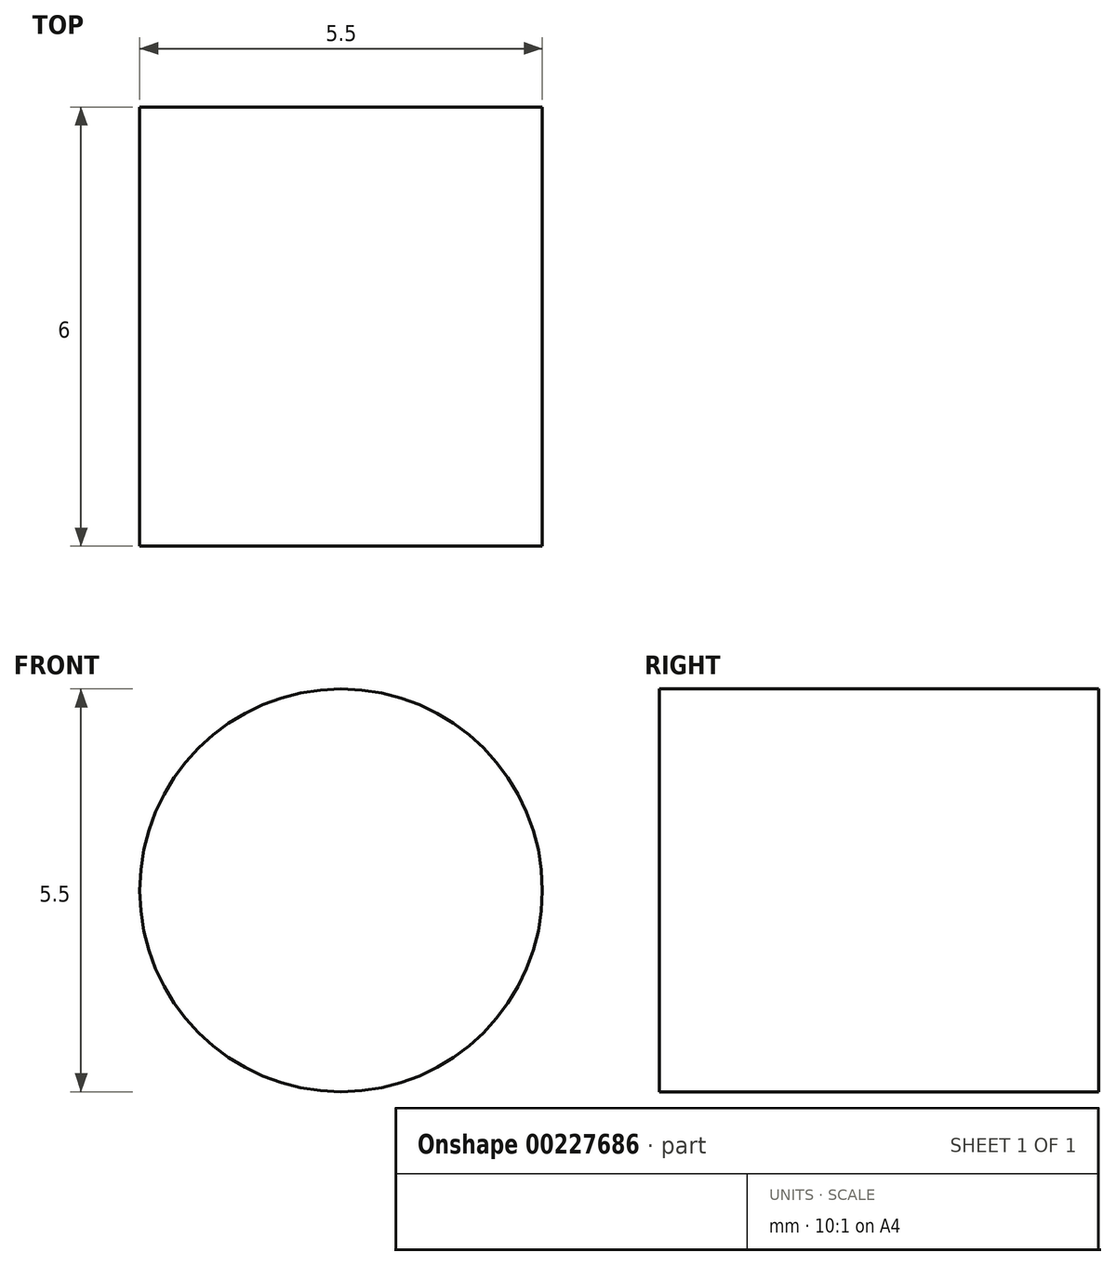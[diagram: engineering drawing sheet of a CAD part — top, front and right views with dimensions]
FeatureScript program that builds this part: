
annotation { "Feature Type Name" : "Feature", "Feature Type Description" : "" }
export const myFeature = defineFeature(function(context is Context, id is Id, definition is map)
    precondition{}
    {
        {
            var Q0;
            Q0=qCreatedBy(makeId("Front.planeOp"),FACE);
            var sketch = newSketch(context, id + "F0", { "sketchPlane" : qUnion([Q0])});
            skLineSegment(sketch, "E0.bottom", {"start": v(229.5, -223.5) * mm, "end": v(-229.5, -223.5) * mm});
            skLineSegment(sketch, "E0.top", {"start": v(229.5, 223.5) * mm, "end": v(-229.5, 223.5) * mm});
            skLineSegment(sketch, "E0.left", {"start": v(229.5, -223.5) * mm, "end": v(229.5, 223.5) * mm});
            skLineSegment(sketch, "E0.right", {"start": v(-229.5, -223.5) * mm, "end": v(-229.5, 223.5) * mm});
            skPoint(sketch, "E0.middle", {"position": v(0, 0) * mm});
            skSolve(sketch);
        }
        {
            var Q0;
            Q0 = qSketchRegion(id + "F0", true);
            extrude(context, id + "F1", {"entities" : qUnion([Q0]), "depth" : 6 * mm, "symmetric" : true});
        }
        {
            var Q0;
            Q0=makeQuery(id+"F1.opExtrude","CAP_FACE",FACE,{"disambiguationData":[OSD([sQuery(id+"F0.wireOp",EDGE,"E0.bottom"),sQuery(id+"F0.wireOp",EDGE,"E0.top"),sQuery(id+"F0.wireOp",EDGE,"E0.left"),sQuery(id+"F0.wireOp",EDGE,"E0.right")])],"isStart":false});
            var sketch = newSketch(context, id + "F2", { "sketchPlane" : qUnion([Q0])});
            skCircle(sketch, "E1", {"center": v(-60, 213.5) * mm, "radius": 2.75 * mm});
            skLineSegment(sketch, "E2", {"start": v(0, 223.5) * mm, "end": v(0, 196.8) * mm});
            skCircle(sketch, "E3.MirrorC", {"center": v(60, 213.5) * mm, "radius": 2.75 * mm});
            skSolve(sketch);
        }
        {
            var Q0;
            Q0=makeQuery(id+"F2.imprint","IMPRINT",FACE,{"disambiguationData":[TD([[makeQuery(id+"F2.imprint","IMPRINT",EDGE,{"derivedFrom":sQuery(id+"F2.wireOp",EDGE,"E1")}),1.0]])]});
            var Q1;
            Q1=makeQuery(id+"F2.imprint","IMPRINT",FACE,{"disambiguationData":[TD([[makeQuery(id+"F2.imprint","IMPRINT",EDGE,{"derivedFrom":sQuery(id+"F2.wireOp",EDGE,"E3.MirrorC")}),-1.0]])]});
            extrude(context, id + "F3", {"entities" : qUnion([Q0, Q1]), "operationType" : NewBodyOperationType.REMOVE, "oppositeDirection" : true, "depth" : 25 * mm});
        }
    });
